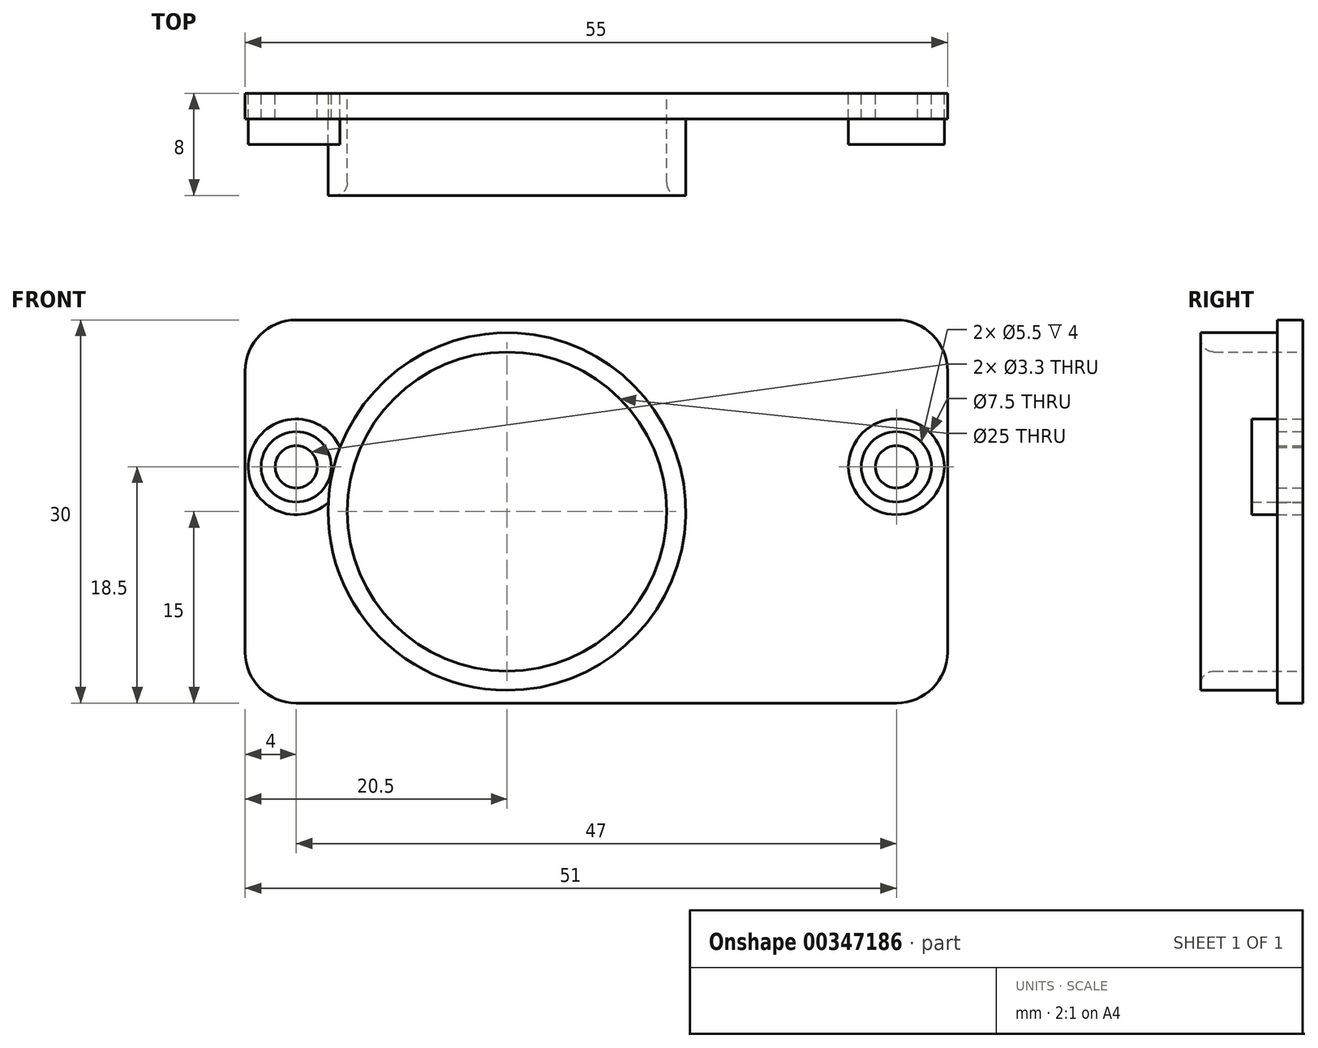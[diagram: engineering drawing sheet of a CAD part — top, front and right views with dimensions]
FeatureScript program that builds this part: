
annotation { "Feature Type Name" : "Feature", "Feature Type Description" : "" }
export const myFeature = defineFeature(function(context is Context, id is Id, definition is map)
    precondition{}
    {
        {
            var Q0;
            Q0=qCreatedBy(makeId("Front.planeOp"),FACE);
            var sketch = newSketch(context, id + "F0", { "sketchPlane" : qUnion([Q0])});
            skLineSegment(sketch, "E0.bottom", {"start": v(23.5, -15) * mm, "end": v(-23.5, -15) * mm});
            skLineSegment(sketch, "E0.top", {"start": v(23.5, 15) * mm, "end": v(-23.5, 15) * mm});
            skLineSegment(sketch, "E0.left", {"start": v(27.5, -11) * mm, "end": v(27.5, 11) * mm});
            skLineSegment(sketch, "E0.right", {"start": v(-27.5, -11) * mm, "end": v(-27.5, 11) * mm});
            skPoint(sketch, "E0.middle", {"position": v(0, 0) * mm});
            skPoint(sketch, "E1.endSnap0", {"position": v(-27.5, 0) * mm});
            skPoint(sketch, "E2", {"position": v(-7, 0) * mm});
            skCircle(sketch, "E3", {"center": v(-7, 0) * mm, "radius": 12.5 * mm});
            skPoint(sketch, "E4", {"position": v(-23.5, 3.5) * mm});
            skPoint(sketch, "E5", {"position": v(23.5, 3.5) * mm});
            skCircle(sketch, "E6", {"center": v(-7, 0) * mm, "radius": 14 * mm});
            skCircle(sketch, "E7", {"center": v(-23.5, 3.5) * mm, "radius": 2.75 * mm});
            skCircle(sketch, "E8", {"center": v(-23.5, 3.5) * mm, "radius": 3.75 * mm});
            skCircle(sketch, "E9", {"center": v(23.5, 3.5) * mm, "radius": 2.75 * mm});
            skCircle(sketch, "E10", {"center": v(23.5, 3.5) * mm, "radius": 3.75 * mm});
            skPoint(sketch, "E11.visualSharp", {"position": v(-27.5, 15) * mm});
            skArc(sketch, "E11.filletArc", {"start": v(-23.5, 15) * mm, "mid": v(-26.33, 13.83) * mm, "end": v(-27.5, 11) * mm});
            skPoint(sketch, "E12.visualSharp", {"position": v(27.5, 15) * mm});
            skArc(sketch, "E12.filletArc", {"start": v(27.5, 11) * mm, "mid": v(26.33, 13.83) * mm, "end": v(23.5, 15) * mm});
            skPoint(sketch, "E13.visualSharp", {"position": v(27.5, -15) * mm});
            skArc(sketch, "E13.filletArc", {"start": v(23.5, -15) * mm, "mid": v(26.33, -13.83) * mm, "end": v(27.5, -11) * mm});
            skPoint(sketch, "E14.visualSharp", {"position": v(-27.5, -15) * mm});
            skArc(sketch, "E14.filletArc", {"start": v(-27.5, -11) * mm, "mid": v(-26.33, -13.83) * mm, "end": v(-23.5, -15) * mm});
            skSolve(sketch);
        }
        {
            var Q0;
            Q0=makeQuery(id+"F0.imprint","IMPRINT",FACE,{"disambiguationData":[TD([[makeQuery(id+"F0.imprint","IMPRINT",EDGE,{"derivedFrom":sQuery(id+"F0.wireOp",EDGE,"E0.bottom")}),-1.0]])]});
            var Q1;
            Q1=makeQuery(id+"F0.imprint","IMPRINT",FACE,{"disambiguationData":[TD([[makeQuery(id+"F0.imprint","IMPRINT",EDGE,{"derivedFrom":sQuery(id+"F0.wireOp",EDGE,"E7")}),1.0]])]});
            var Q2;
            Q2=makeQuery(id+"F0.imprint","IMPRINT",FACE,{"disambiguationData":[TD([[makeQuery(id+"F0.imprint","IMPRINT",EDGE,{"derivedFrom":sQuery(id+"F0.wireOp",EDGE,"E9")}),1.0]])]});
            extrude(context, id + "F1", {"entities" : qUnion([Q0, Q1, Q2]), "depth" : 2 * mm});
        }
        {
            var Q0;
            Q0=makeQuery(id+"F0.imprint","IMPRINT",FACE,{"disambiguationData":[TD([[makeQuery(id+"F0.imprint","IMPRINT",EDGE,{"derivedFrom":sQuery(id+"F0.wireOp",EDGE,"E3")}),-1.0]])]});
            var Q1;
            {var subQ0=sQuery(id+"F0.wireOp",EDGE,"E8");var subQ1=sQuery(id+"F0.wireOp",EDGE,"E6");var subQ2=makeQuery(id+"F0.imprint","INTERSECT",VERTEX,{"disambiguationData":[OD(0.0)],"derivedFrom":[subQ1,subQ0]});Q1=makeQuery(id+"F0.imprint","IMPRINT",FACE,{"disambiguationData":[TD([[makeQuery(id+"F0.imprint","IMPRINT",EDGE,{"disambiguationData":[TD([[subQ2,1.0]])],"derivedFrom":subQ1}),1.0]])]});}
            extrude(context, id + "F2", {"entities" : qUnion([Q0, Q1]), "operationType" : NewBodyOperationType.ADD, "depth" : 8 * mm});
        }
        {
            var Q0;
            Q0=makeQuery(id+"F0.imprint","IMPRINT",FACE,{"disambiguationData":[TD([[makeQuery(id+"F0.imprint","IMPRINT",EDGE,{"derivedFrom":sQuery(id+"F0.wireOp",EDGE,"E7")}),-1.0]])]});
            var Q1;
            Q1=makeQuery(id+"F0.imprint","IMPRINT",FACE,{"disambiguationData":[TD([[makeQuery(id+"F0.imprint","IMPRINT",EDGE,{"derivedFrom":sQuery(id+"F0.wireOp",EDGE,"E9")}),-1.0]])]});
            extrude(context, id + "F3", {"entities" : qUnion([Q0, Q1]), "depth" : 4 * mm});
        }
        {
            var Q0;
            Q0=makeQuery(id+"F2.opExtrude","CAP_EDGE",EDGE,{"disambiguationData":[OSD([sQuery(id+"F0.wireOp",EDGE,"E3")])],"isStart":false});
            fillet(context, id + "F4", {"entities" : qUnion([Q0]), "radius" : 1 * mm, "tangentPropagation" : true, "allowEdgeOverflow" : false});
        }
        {
            var Q0;
            Q0=sQuery(id+"F0.wireOp",VERTEX,"E4");
            var Q1;
            Q1=sQuery(id+"F0.wireOp",VERTEX,"E5");
            var Q2;
            Q2=makeQuery(id+"F1.opExtrude","SWEPT_BODY",BODY,{"disambiguationData":[OSD([sQuery(id+"F0.wireOp",EDGE,"E7")])]});
            var Q3;
            Q3=makeQuery(id+"F1.opExtrude","SWEPT_BODY",BODY,{"disambiguationData":[OSD([sQuery(id+"F0.wireOp",EDGE,"E9")])]});
            hole(context, id + "F5", {"style" : HoleStyle.SIMPLE, "endStyle" : HoleEndStyle.BLIND, "oppositeDirection" : true, "standardTappedOrClearance" : lookupTablePath({ "standard" : "ISO", "fit" : "Normal", "size" : "M3", "type" : "Clearance" }), "standardBlindInLast" : lookupTablePath({ "fit" : "Standard", "standard" : "ISO", "size" : "M3", "type" : "Clearance" }), "holeDiameter" : 3.3 * mm, "holeDepth" : 7.9 * mm, "tappedDepth" : 5.5 * mm, "tapClearance" : 3, "locations" : qUnion([Q0, Q1]), "scope" : qUnion([Q2, Q3])});
        }
    });
